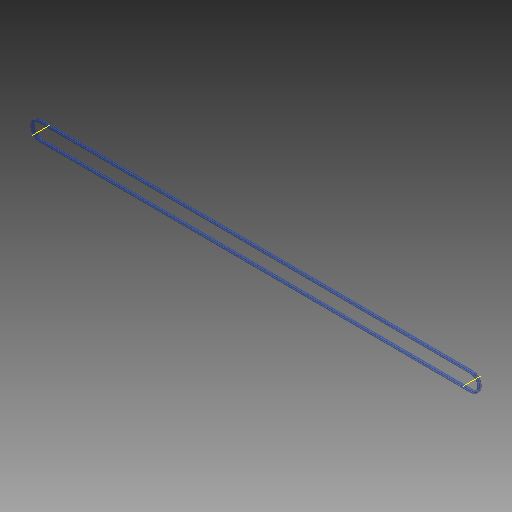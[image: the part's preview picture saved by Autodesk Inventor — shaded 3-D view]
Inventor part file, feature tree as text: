
AUTODESK INVENTOR PART (.ipt)
format: ipt  version: 2017 (Build 210142000, 142)  size: 136,704 bytes
history: native  units: mm
features: other x5, plane x2, pattern_linear x1
ambient origin geometry x8: Origin, YZ Plane, XZ Plane, XY Plane, X Axis, Y Axis, Z Axis, Center Point
bodies: Solid1 (feature_tree), Solid (feature_tree)
feature tree (8):
  other  "Work Axis1"
  other  "Work Axis2"
  plane  "Work Plane2"
  plane  "Work Plane3"
  other  "Path"
  other  "Section Plane"
  pattern_linear  "Strand Pattern"  Spacing1=0.0mm  [1 undecoded]
  other  "Section Sketch"
note: 1 required parameter value undecoded (feature->parameter linkage not recoverable at this tier; creation-order binding heuristic only, values carry confidence <= 0.55)
